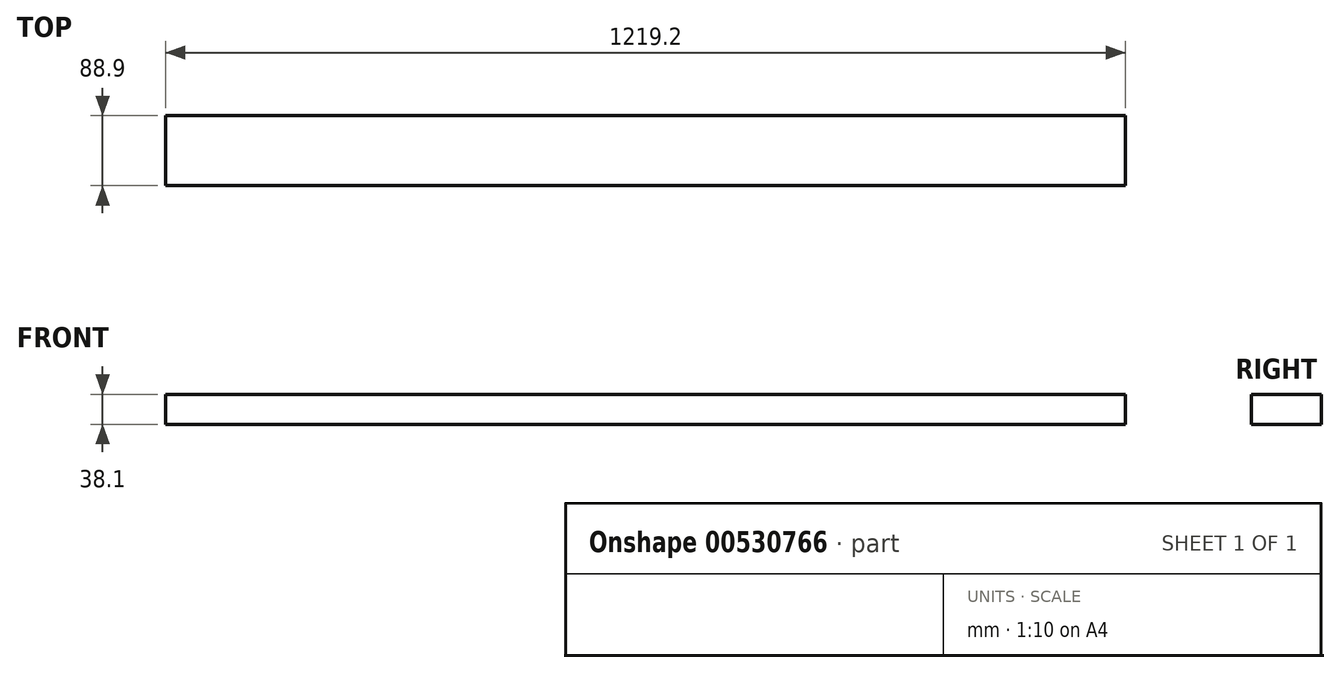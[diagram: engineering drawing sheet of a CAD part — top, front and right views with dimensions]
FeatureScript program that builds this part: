
annotation { "Feature Type Name" : "Feature", "Feature Type Description" : "" }
export const myFeature = defineFeature(function(context is Context, id is Id, definition is map)
    precondition{}
    {
        {
            var Q0;
            Q0=qCreatedBy(makeId("Front.planeOp"),FACE);
            var sketch = newSketch(context, id + "F0", { "sketchPlane" : qUnion([Q0])});
            skLineSegment(sketch, "E0", {"start": v(0, 0) * mm, "end": v(-1219.2, 0) * mm});
            skLineSegment(sketch, "E1", {"start": v(-1219.2, 0) * mm, "end": v(-1219.2, 38.1) * mm});
            skLineSegment(sketch, "E2", {"start": v(-1219.2, 38.1) * mm, "end": v(0, 38.1) * mm});
            skLineSegment(sketch, "E3", {"start": v(0, 38.1) * mm, "end": v(0, 0) * mm});
            skSolve(sketch);
        }
        {
            var Q0;
            Q0 = qSketchRegion(id + "F0", true);
            extrude(context, id + "F1", {"entities" : qUnion([Q0]), "depth" : 88.9 * mm, "offsetDistance" : 25.4 * mm});
        }
    });
